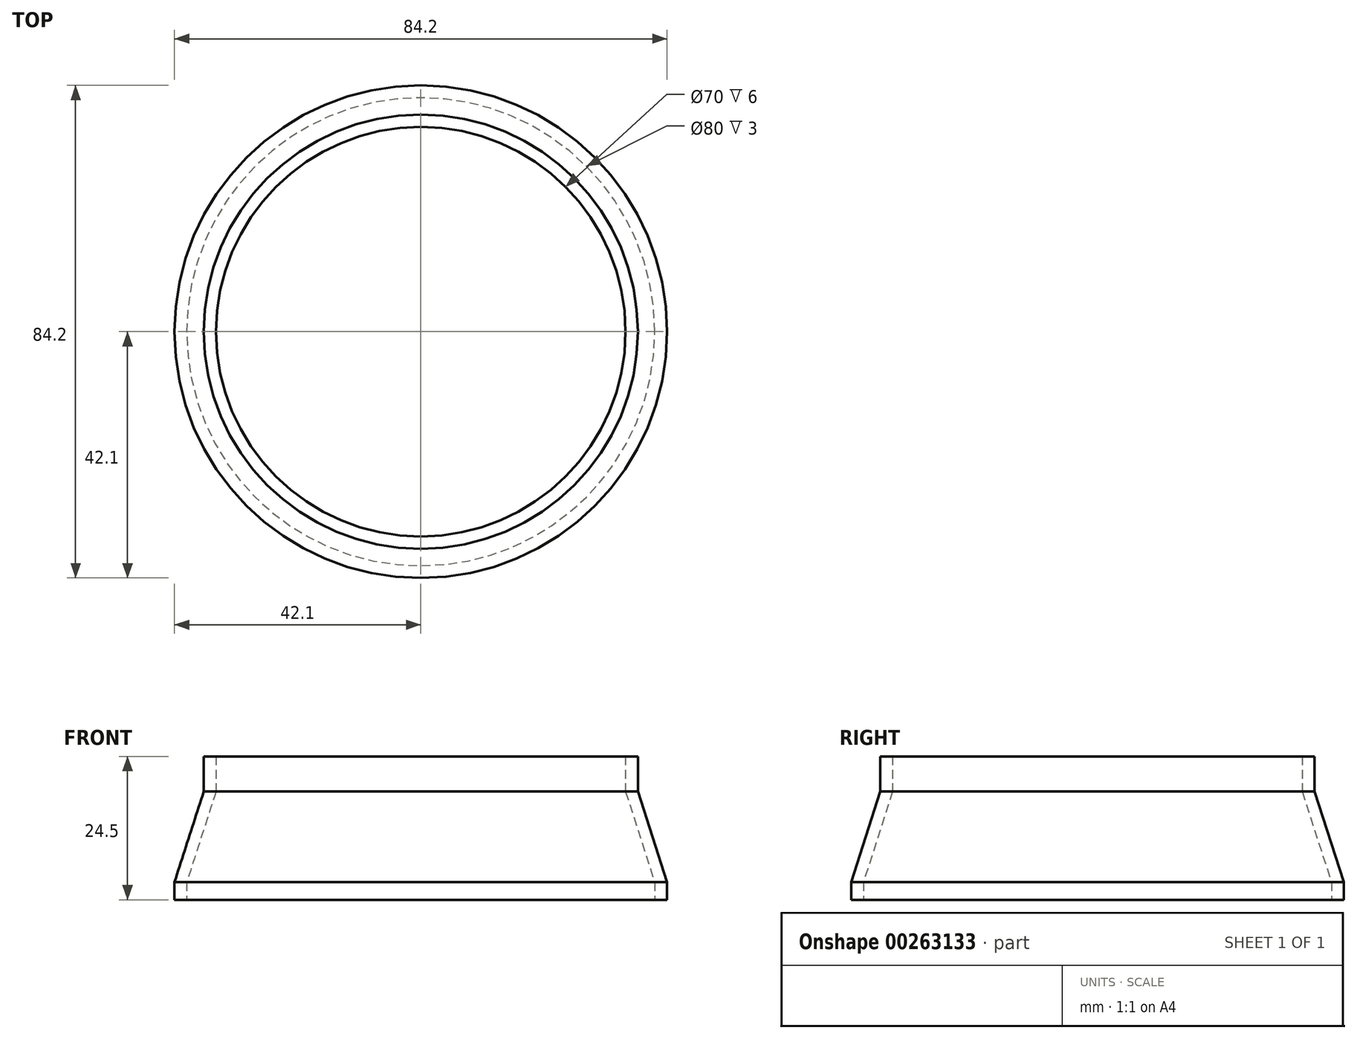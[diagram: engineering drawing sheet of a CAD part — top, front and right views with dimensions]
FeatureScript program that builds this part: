
annotation { "Feature Type Name" : "Feature", "Feature Type Description" : "" }
export const myFeature = defineFeature(function(context is Context, id is Id, definition is map)
    precondition{}
    {
        {
            var Q0;
            Q0=qCreatedBy(makeId("Front.planeOp"),FACE);
            var sketch = newSketch(context, id + "F0", { "sketchPlane" : qUnion([Q0])});
            skLineSegment(sketch, "E0", {"start": v(0, 0) * mm, "end": v(0, 15.5) * mm});
            skLineSegment(sketch, "E1", {"start": v(0, 0) * mm, "end": v(40, 0) * mm});
            skLineSegment(sketch, "E2", {"start": v(0, 15.5) * mm, "end": v(35, 15.5) * mm});
            skLineSegment(sketch, "E3", {"start": v(35, 15.5) * mm, "end": v(40, 0) * mm});
            skLineSegment(sketch, "E4.0", {"start": v(37.1, 15.5) * mm, "end": v(42.1, 0) * mm});
            skLineSegment(sketch, "E5", {"start": v(35, 15.5) * mm, "end": v(37.1, 15.5) * mm});
            skLineSegment(sketch, "E6", {"start": v(40, 0) * mm, "end": v(42.1, 0) * mm});
            skLineSegment(sketch, "E7", {"start": v(35, 15.5) * mm, "end": v(35, 21.5) * mm});
            skLineSegment(sketch, "E8", {"start": v(37.1, 15.5) * mm, "end": v(37.1, 21.5) * mm});
            skLineSegment(sketch, "E9", {"start": v(35, 21.5) * mm, "end": v(37.1, 21.5) * mm});
            skLineSegment(sketch, "E10", {"start": v(40, 0) * mm, "end": v(40, -3) * mm});
            skLineSegment(sketch, "E11", {"start": v(42.1, 0) * mm, "end": v(42.1, -3) * mm});
            skLineSegment(sketch, "E12", {"start": v(42.1, -3) * mm, "end": v(40, -3) * mm});
            skSolve(sketch);
        }
        {
            var Q0;
            Q0=makeQuery(id+"F0.imprint","IMPRINT",FACE,{"disambiguationData":[TD([[makeQuery(id+"F0.imprint","IMPRINT",EDGE,{"derivedFrom":sQuery(id+"F0.wireOp",EDGE,"E5")}),1.0]])]});
            var Q1;
            Q1=makeQuery(id+"F0.imprint","IMPRINT",FACE,{"disambiguationData":[TD([[makeQuery(id+"F0.imprint","IMPRINT",EDGE,{"derivedFrom":sQuery(id+"F0.wireOp",EDGE,"E3")}),1.0]])]});
            var Q2;
            Q2=makeQuery(id+"F0.imprint","IMPRINT",FACE,{"disambiguationData":[TD([[makeQuery(id+"F0.imprint","IMPRINT",EDGE,{"derivedFrom":sQuery(id+"F0.wireOp",EDGE,"E6")}),-1.0]])]});
            var Q3;
            Q3=sQuery(id+"F0.wireOp",EDGE,"E0");
            revolve(context, id + "F1", {"entities" : qUnion([Q0, Q1, Q2]), "axis" : qUnion([Q3]), "revolveType" : RevolveType.FULL});
        }
    });
